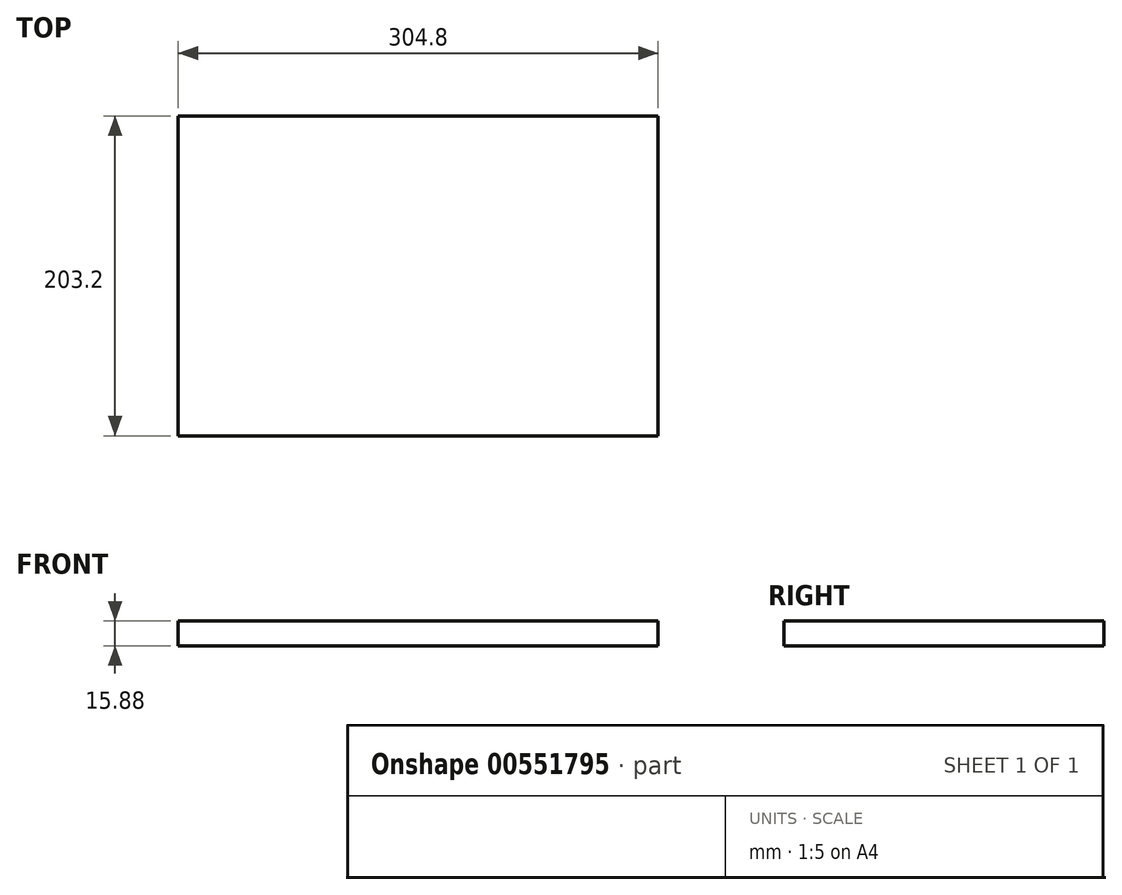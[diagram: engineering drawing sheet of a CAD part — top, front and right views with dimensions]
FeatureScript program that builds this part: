
annotation { "Feature Type Name" : "Feature", "Feature Type Description" : "" }
export const myFeature = defineFeature(function(context is Context, id is Id, definition is map)
    precondition{}
    {
        {
            var Q0;
            Q0=qCreatedBy(makeId("Top.planeOp"),FACE);
            var sketch = newSketch(context, id + "F0", { "sketchPlane" : qUnion([Q0])});
            skLineSegment(sketch, "E0.bottom", {"start": v(-154.08, 124.3) * mm, "end": v(150.72, 124.3) * mm});
            skLineSegment(sketch, "E0.top", {"start": v(-154.08, -78.9) * mm, "end": v(150.72, -78.9) * mm});
            skLineSegment(sketch, "E0.left", {"start": v(-154.08, 124.3) * mm, "end": v(-154.08, -78.9) * mm});
            skLineSegment(sketch, "E0.right", {"start": v(150.72, 124.3) * mm, "end": v(150.72, -78.9) * mm});
            skSolve(sketch);
        }
        {
            var Q0;
            Q0 = qSketchRegion(id + "F0", true);
            extrude(context, id + "F1", {"entities" : qUnion([Q0]), "depth" : 15.88 * mm, "offsetDistance" : 25.4 * mm});
        }
    });
